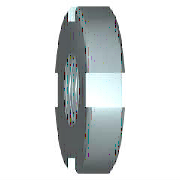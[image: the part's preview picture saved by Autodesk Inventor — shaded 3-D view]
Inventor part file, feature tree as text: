
AUTODESK INVENTOR PART (.ipt)
format: ipt  version: 2020 (Build 240168000, 168)  size: 195,584 bytes
history: native  units: mm (DEFAULTED — no unit token found)
features: sketch x3, other x2, hole x1, extrude x1, pattern_circular x1, plane x1
ambient origin geometry x8: Origin, YZ Plane, XZ Plane, XY Plane, X Axis, Y Axis, Z Axis, Center Point
bodies: Solid1 (feature_tree)
feature tree (9):
  other  "轴承体"
  hole  "螺纹"  [1 undecoded]
  extrude  "沟槽1"  Depth=10.0mm
  pattern_circular  "IDS_ARRAYGROOVE{1}"  Angle=45.0deg  [1 undecoded]
  other  "Work Axis1"
  plane  "Work Plane1"
  sketch  "草图1"  dims[d0=90.0deg d1=45.0mm]
  sketch  "草图2"  dims[d2=8.0mm]
  sketch  "草图3"  dims[d3=28.376mm d4=6.0mm d5=4.0mm d6=2.0mm d7=14.3117mm d8=8.0mm d9=0.0mm d10=1.0mm d11=45.0deg d12=2.5mm d13=2.5mm d14=20.0mm d23=10.0mm d15=0.0mm d16=40.0mm d17=360.0deg d18=0.75mm d19=30.0deg d20=0.75mm d21=30.0deg d22=0.0mm d24=0.0mm d25=1.0mm d27=45.0deg d28=0.0mm d41=1.0mm d42=1.0mm d43=0.75mm d44=0.75mm d45=90.0deg d46=0.0mm]
note: 2 required parameter values undecoded (feature->parameter linkage not recoverable at this tier; creation-order binding heuristic only, values carry confidence <= 0.55)
